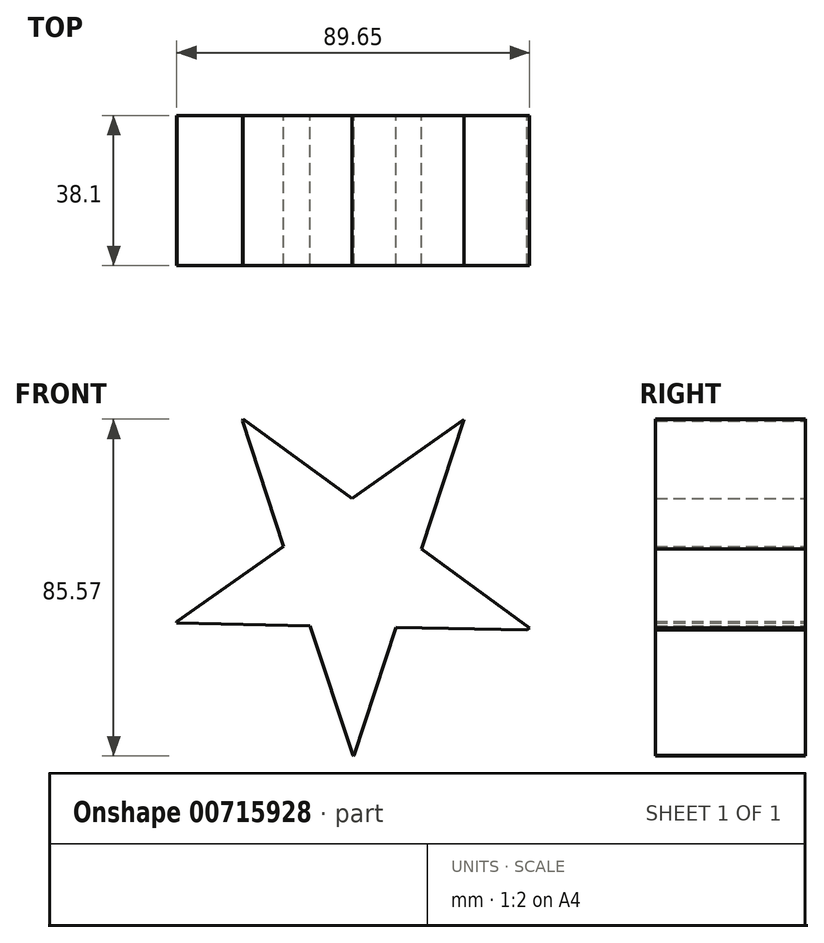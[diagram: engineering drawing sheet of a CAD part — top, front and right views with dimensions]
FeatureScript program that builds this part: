
annotation { "Feature Type Name" : "Feature", "Feature Type Description" : "" }
export const myFeature = defineFeature(function(context is Context, id is Id, definition is map)
    precondition{}
    {
        {
            var Q0;
            Q0=qCreatedBy(makeId("Front.planeOp"),FACE);
            var sketch = newSketch(context, id + "F0", { "sketchPlane" : qUnion([Q0])});
            skCircle(sketch, "E0.cCircle", {"center": v(0, 0) * mm, "radius": 38.42 * mm, "construction": true});
            skLineSegment(sketch, "E0.0", {"start": v(-27.92, 38.42) * mm, "end": v(27.92, 38.42) * mm});
            skLineSegment(sketch, "E0.1", {"start": v(27.92, 38.42) * mm, "end": v(45.17, -14.68) * mm});
            skLineSegment(sketch, "E0.2", {"start": v(45.17, -14.68) * mm, "end": v(0, -47.5) * mm});
            skLineSegment(sketch, "E0.3", {"start": v(0, -47.5) * mm, "end": v(-45.17, -14.68) * mm});
            skLineSegment(sketch, "E0.4", {"start": v(-45.17, -14.68) * mm, "end": v(-27.92, 38.42) * mm});
            skPoint(sketch, "E0.0.midPoint", {"position": v(0, 38.42) * mm});
            skSolve(sketch);
        }
        {
            var Q0;
            Q0=makeQuery(id+"F0.imprint","IMPRINT",FACE,{"disambiguationData":[TD([[makeQuery(id+"F0.imprint","IMPRINT",EDGE,{"derivedFrom":sQuery(id+"F0.wireOp",EDGE,"E0.0")}),-1.0]])]});
            var sketch = newSketch(context, id + "F1", { "sketchPlane" : qUnion([Q0])});
            skLineSegment(sketch, "E1", {"start": v(28.05, 37.99) * mm, "end": v(0, -47.8) * mm});
            skLineSegment(sketch, "E2", {"start": v(0, -47.8) * mm, "end": v(-28.49, 38.42) * mm});
            skLineSegment(sketch, "E3", {"start": v(-28.49, 38.42) * mm, "end": v(45.52, -15.5) * mm});
            skLineSegment(sketch, "E4", {"start": v(45.52, -15.5) * mm, "end": v(-45.3, -13.75) * mm});
            skLineSegment(sketch, "E5", {"start": v(-45.3, -13.75) * mm, "end": v(28.05, 37.99) * mm});
            skSolve(sketch);
        }
        {
            var Q0;
            {var subQ3=sQuery(id+"F1.wireOp",EDGE,"E1");var subQ5=sQuery(id+"F1.wireOp",EDGE,"E4");var subQ6=makeQuery(id+"F1.imprint","INTERSECT",VERTEX,{"derivedFrom":[subQ3,subQ5]});Q0=makeQuery(id+"F1.imprint","IMPRINT",FACE,{"disambiguationData":[TD([[makeQuery(id+"F1.imprint","IMPRINT",EDGE,{"disambiguationData":[TD([[subQ6,-1.0]])],"derivedFrom":subQ3}),-1.0]])]});}
            var Q1;
            {var subQ0=sQuery(id+"F1.wireOp",EDGE,"E3");var subQ1=sQuery(id+"F1.wireOp",EDGE,"E1");var subQ2=makeQuery(id+"F1.imprint","INTERSECT",VERTEX,{"derivedFrom":[subQ1,subQ0]});Q1=makeQuery(id+"F1.imprint","IMPRINT",FACE,{"disambiguationData":[TD([[makeQuery(id+"F1.imprint","IMPRINT",EDGE,{"disambiguationData":[TD([[subQ2,-1.0]])],"derivedFrom":subQ1}),1.0]])]});}
            var Q2;
            {var subQ0=sQuery(id+"F1.wireOp",EDGE,"E5");var subQ1=sQuery(id+"F1.wireOp",EDGE,"E2");var subQ2=makeQuery(id+"F1.imprint","INTERSECT",VERTEX,{"derivedFrom":[subQ1,subQ0]});Q2=makeQuery(id+"F1.imprint","IMPRINT",FACE,{"disambiguationData":[TD([[makeQuery(id+"F1.imprint","IMPRINT",EDGE,{"disambiguationData":[TD([[subQ2,-1.0]])],"derivedFrom":subQ1}),-1.0]])]});}
            var Q3;
            {var subQ0=sQuery(id+"F1.wireOp",EDGE,"E4");var subQ1=sQuery(id+"F1.wireOp",EDGE,"E2");var subQ2=makeQuery(id+"F1.imprint","INTERSECT",VERTEX,{"derivedFrom":[subQ1,subQ0]});Q3=makeQuery(id+"F1.imprint","IMPRINT",FACE,{"disambiguationData":[TD([[makeQuery(id+"F1.imprint","IMPRINT",EDGE,{"disambiguationData":[TD([[subQ2,-1.0]])],"derivedFrom":subQ1}),1.0]])]});}
            var Q4;
            {var subQ0=sQuery(id+"F1.wireOp",EDGE,"E5");var subQ1=sQuery(id+"F1.wireOp",EDGE,"E1");var subQ2=makeQuery(id+"F1.imprint","INTERSECT",VERTEX,{"derivedFrom":[subQ1,subQ0]});Q4=makeQuery(id+"F1.imprint","IMPRINT",FACE,{"disambiguationData":[TD([[makeQuery(id+"F1.imprint","IMPRINT",EDGE,{"disambiguationData":[TD([[subQ2,-1.0]])],"derivedFrom":subQ1}),-1.0]])]});}
            var Q5;
            {var subQ1=sQuery(id+"F1.wireOp",EDGE,"E1");var subQ5=sQuery(id+"F1.wireOp",EDGE,"E3");var subQ6=makeQuery(id+"F1.imprint","INTERSECT",VERTEX,{"derivedFrom":[subQ1,subQ5]});Q5=makeQuery(id+"F1.imprint","IMPRINT",FACE,{"disambiguationData":[TD([[makeQuery(id+"F1.imprint","IMPRINT",EDGE,{"disambiguationData":[TD([[subQ6,-1.0]])],"derivedFrom":subQ1}),-1.0]])]});}
            extrude(context, id + "F2", {"entities" : qUnion([Q0, Q1, Q2, Q3, Q4, Q5]), "depth" : 38.1 * mm, "offsetDistance" : 25.4 * mm});
        }
    });
